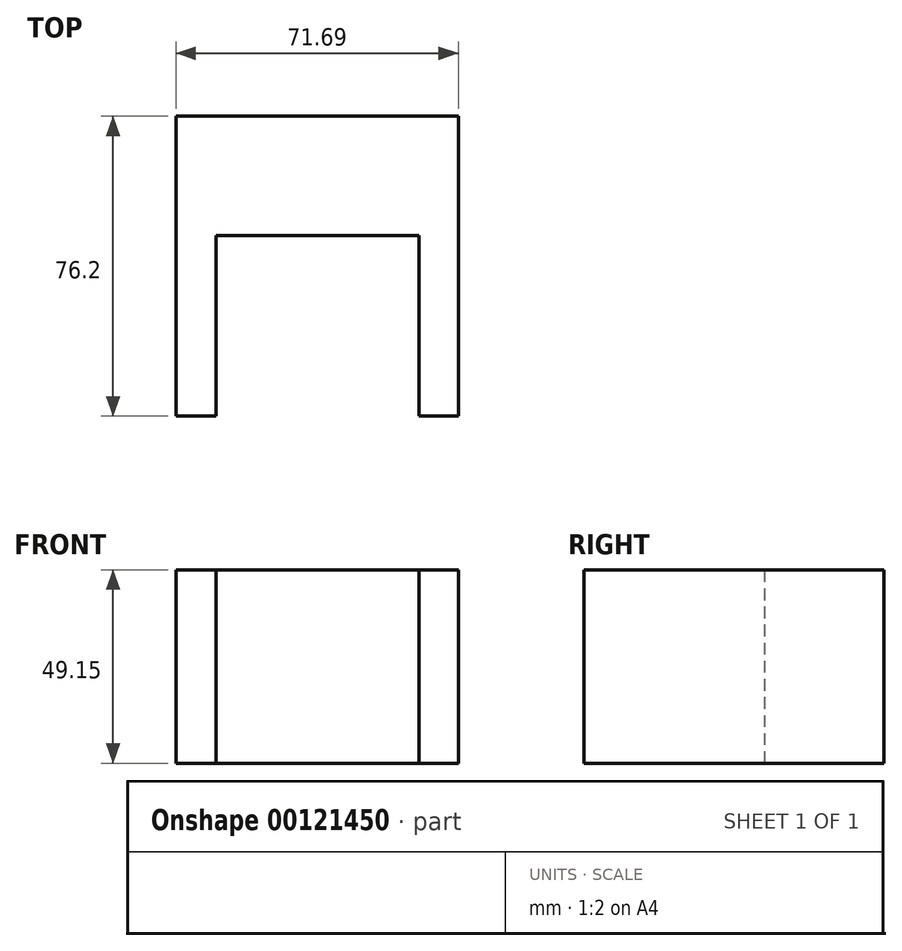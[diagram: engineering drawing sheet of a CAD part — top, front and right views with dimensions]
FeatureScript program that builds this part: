
annotation { "Feature Type Name" : "Feature", "Feature Type Description" : "" }
export const myFeature = defineFeature(function(context is Context, id is Id, definition is map)
    precondition{}
    {
        {
            var Q0;
            Q0=qCreatedBy(makeId("Front.planeOp"),FACE);
            var sketch = newSketch(context, id + "F0", { "sketchPlane" : qUnion([Q0])});
            skLineSegment(sketch, "E0", {"start": v(0, 0) * mm, "end": v(0, 49.15) * mm});
            skLineSegment(sketch, "E1", {"start": v(0, 49.15) * mm, "end": v(71.69, 49.15) * mm});
            skLineSegment(sketch, "E2", {"start": v(71.69, 49.15) * mm, "end": v(71.69, 0) * mm});
            skLineSegment(sketch, "E3", {"start": v(71.69, 0) * mm, "end": v(0, 0) * mm});
            skSolve(sketch);
        }
        {
            var Q0;
            Q0=makeQuery(id+"F0.imprint","IMPRINT",FACE,{"disambiguationData":[TD([[makeQuery(id+"F0.imprint","IMPRINT",EDGE,{"derivedFrom":sQuery(id+"F0.wireOp",EDGE,"E0")}),-1.0]])]});
            extrude(context, id + "F1", {"entities" : qUnion([Q0]), "depth" : 76.2 * mm});
        }
        {
            var Q0;
            Q0=makeQuery(id+"F1.opExtrude","SWEPT_FACE",FACE,{"disambiguationData":[OSD([sQuery(id+"F0.wireOp",EDGE,"E1")])]});
            var sketch = newSketch(context, id + "F2", { "sketchPlane" : qUnion([Q0])});
            skLineSegment(sketch, "E4.bottom", {"start": v(10.14, -30.24) * mm, "end": v(61.75, -30.24) * mm});
            skLineSegment(sketch, "E4.top", {"start": v(10.14, -76.2) * mm, "end": v(61.75, -76.2) * mm});
            skLineSegment(sketch, "E4.left", {"start": v(10.14, -30.24) * mm, "end": v(10.14, -76.2) * mm});
            skLineSegment(sketch, "E4.right", {"start": v(61.75, -30.24) * mm, "end": v(61.75, -76.2) * mm});
            skSolve(sketch);
        }
        {
            var Q0;
            Q0=makeQuery(id+"F2.imprint","IMPRINT",FACE,{"disambiguationData":[TD([[makeQuery(id+"F2.imprint","IMPRINT",EDGE,{"derivedFrom":sQuery(id+"F2.wireOp",EDGE,"E4.bottom")}),-1.0]])]});
            extrude(context, id + "F3", {"entities" : qUnion([Q0]), "operationType" : NewBodyOperationType.REMOVE, "oppositeDirection" : true, "depth" : 50.8 * mm});
        }
    });
